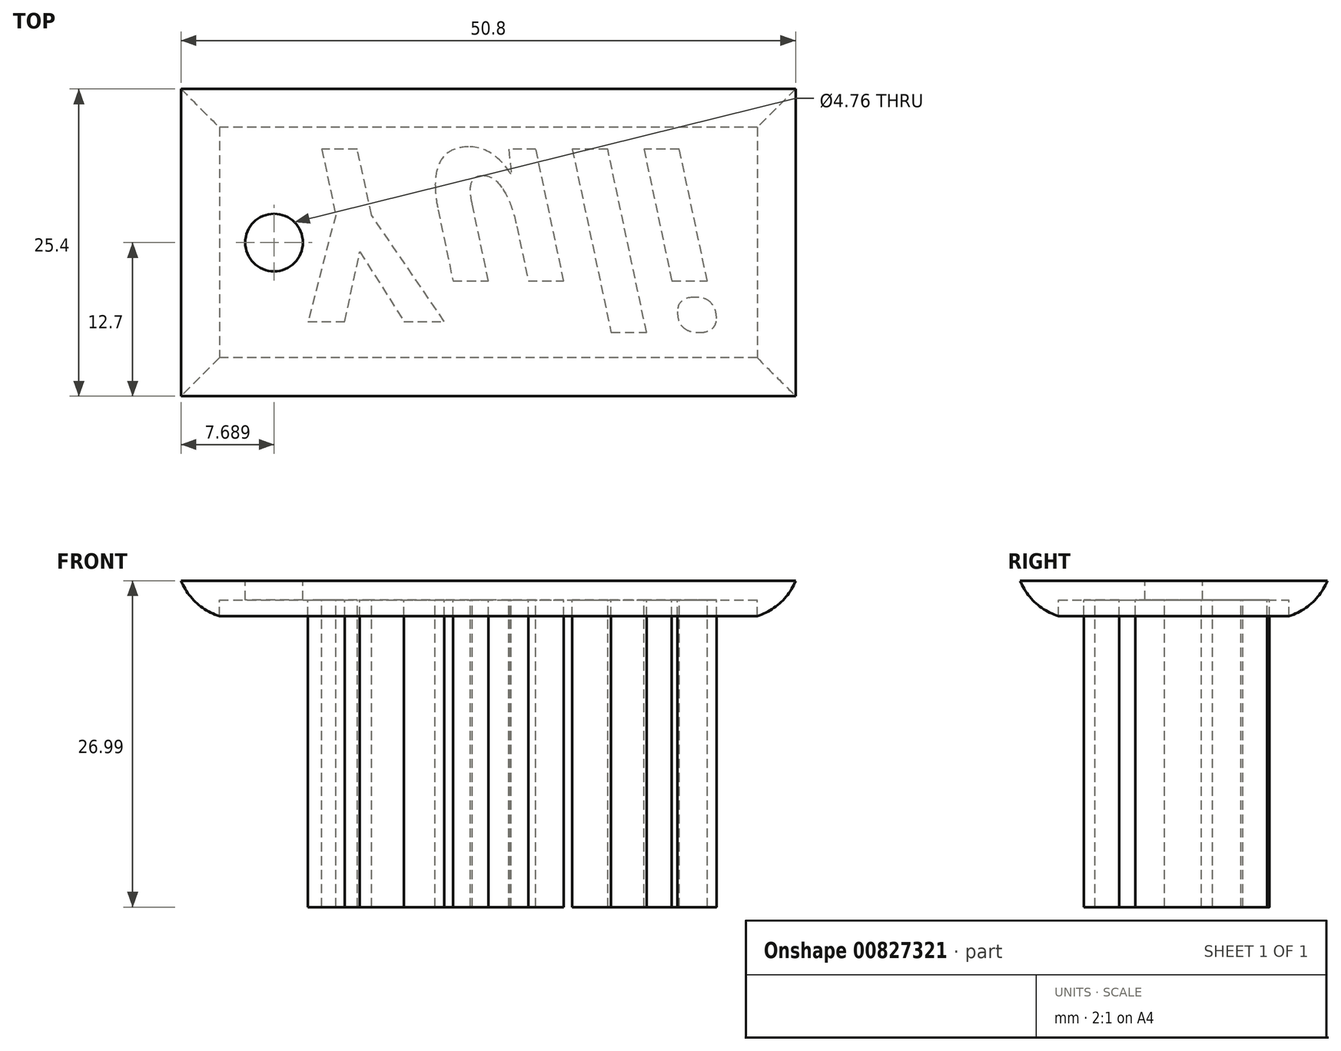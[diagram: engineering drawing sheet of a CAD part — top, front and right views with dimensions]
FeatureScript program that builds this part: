
annotation { "Feature Type Name" : "Feature", "Feature Type Description" : "" }
export const myFeature = defineFeature(function(context is Context, id is Id, definition is map)
    precondition{}
    {
        {
            var Q0;
            Q0=qCreatedBy(makeId("Top.planeOp"),FACE);
            var sketch = newSketch(context, id + "F0", { "sketchPlane" : qUnion([Q0])});
            skLineSegment(sketch, "E0.bottom", {"start": v(0, 0) * mm, "end": v(50.8, 0) * mm});
            skLineSegment(sketch, "E0.top", {"start": v(0, 25.4) * mm, "end": v(50.8, 25.4) * mm});
            skLineSegment(sketch, "E0.left", {"start": v(0, 0) * mm, "end": v(0, 25.4) * mm});
            skLineSegment(sketch, "E0.right", {"start": v(50.8, 0) * mm, "end": v(50.8, 25.4) * mm});
            skPoint(sketch, "E1.centerSnap0", {"position": v(0, 12.7) * mm});
            skCircle(sketch, "E2", {"center": v(7.69, 12.7) * mm, "radius": 2.38 * mm});
            skLineSegment(sketch, "E3.0", {"start": v(3.17, 22.23) * mm, "end": v(47.62, 22.23) * mm});
            skLineSegment(sketch, "E3.1", {"start": v(3.18, 3.18) * mm, "end": v(3.17, 22.23) * mm});
            skLineSegment(sketch, "E3.2", {"start": v(3.17, 3.18) * mm, "end": v(47.62, 3.18) * mm});
            skLineSegment(sketch, "E3.3", {"start": v(47.62, 3.18) * mm, "end": v(47.62, 22.23) * mm});
            skSolve(sketch);
        }
        {
            var Q0;
            Q0=makeQuery(id+"F0.imprint","IMPRINT",FACE,{"disambiguationData":[TD([[makeQuery(id+"F0.imprint","IMPRINT",EDGE,{"derivedFrom":sQuery(id+"F0.wireOp",EDGE,"E0.bottom")}),1.0]])]});
            extrude(context, id + "F1", {"entities" : qUnion([Q0]), "oppositeDirection" : true, "depth" : 3.17 * mm, "offsetDistance" : 25.4 * mm});
        }
        {
            var Q0;
            Q0=makeQuery(id+"F0.imprint","IMPRINT",FACE,{"disambiguationData":[TD([[makeQuery(id+"F0.imprint","IMPRINT",EDGE,{"derivedFrom":sQuery(id+"F0.wireOp",EDGE,"E2")}),-1.0]])]});
            extrude(context, id + "F2", {"entities" : qUnion([Q0]), "operationType" : NewBodyOperationType.ADD, "oppositeDirection" : true, "depth" : 1.59 * mm, "offsetDistance" : 25.4 * mm});
        }
        {
            var Q0;
            Q0=makeQuery(id+"F1.opExtrude","CAP_EDGE",EDGE,{"disambiguationData":[OSD([sQuery(id+"F0.wireOp",EDGE,"E0.top")])],"isStart":false});
            var Q1;
            Q1=makeQuery(id+"F1.opExtrude","CAP_EDGE",EDGE,{"disambiguationData":[OSD([sQuery(id+"F0.wireOp",EDGE,"E0.right")])],"isStart":false});
            var Q2;
            Q2=makeQuery(id+"F1.opExtrude","CAP_EDGE",EDGE,{"disambiguationData":[OSD([sQuery(id+"F0.wireOp",EDGE,"E0.bottom")])],"isStart":false});
            var Q3;
            Q3=makeQuery(id+"F1.opExtrude","CAP_EDGE",EDGE,{"disambiguationData":[OSD([sQuery(id+"F0.wireOp",EDGE,"E0.left")])],"isStart":false});
            fillet(context, id + "F3", {"entities" : qUnion([Q0, Q1, Q2, Q3]), "radius" : 5.08 * mm, "tangentPropagation" : true, "allowEdgeOverflow" : false});
        }
        {
            var Q0;
            Q0=makeQuery(id+"F2.opExtrude","CAP_FACE",FACE,{"disambiguationData":[OSD([sQuery(id+"F0.wireOp",EDGE,"E2"),sQuery(id+"F0.wireOp",EDGE,"E3.0"),sQuery(id+"F0.wireOp",EDGE,"E3.1"),sQuery(id+"F0.wireOp",EDGE,"E3.2"),sQuery(id+"F0.wireOp",EDGE,"E3.3")])],"isStart":false});
            var sketch = newSketch(context, id + "F4", { "sketchPlane" : qUnion([Q0])});
            skText(sketch, "E4", { "text": "Yuli\n", "fontName": "OpenSans-BoldItalic.ttf"});
            const initialGuessF4  = {"E4": [0.00868, -0.02042, 1, 0, 0.01436]};
            skSetInitialGuess(sketch, initialGuessF4);
            skSolve(sketch);
        }
        {
            var Q0;
            Q0 = qSketchRegion(id + "F4", true);
            extrude(context, id + "F5", {"entities" : qUnion([Q0]), "operationType" : NewBodyOperationType.ADD, "depth" : 25.4 * mm, "offsetDistance" : 25.4 * mm});
        }
    });
